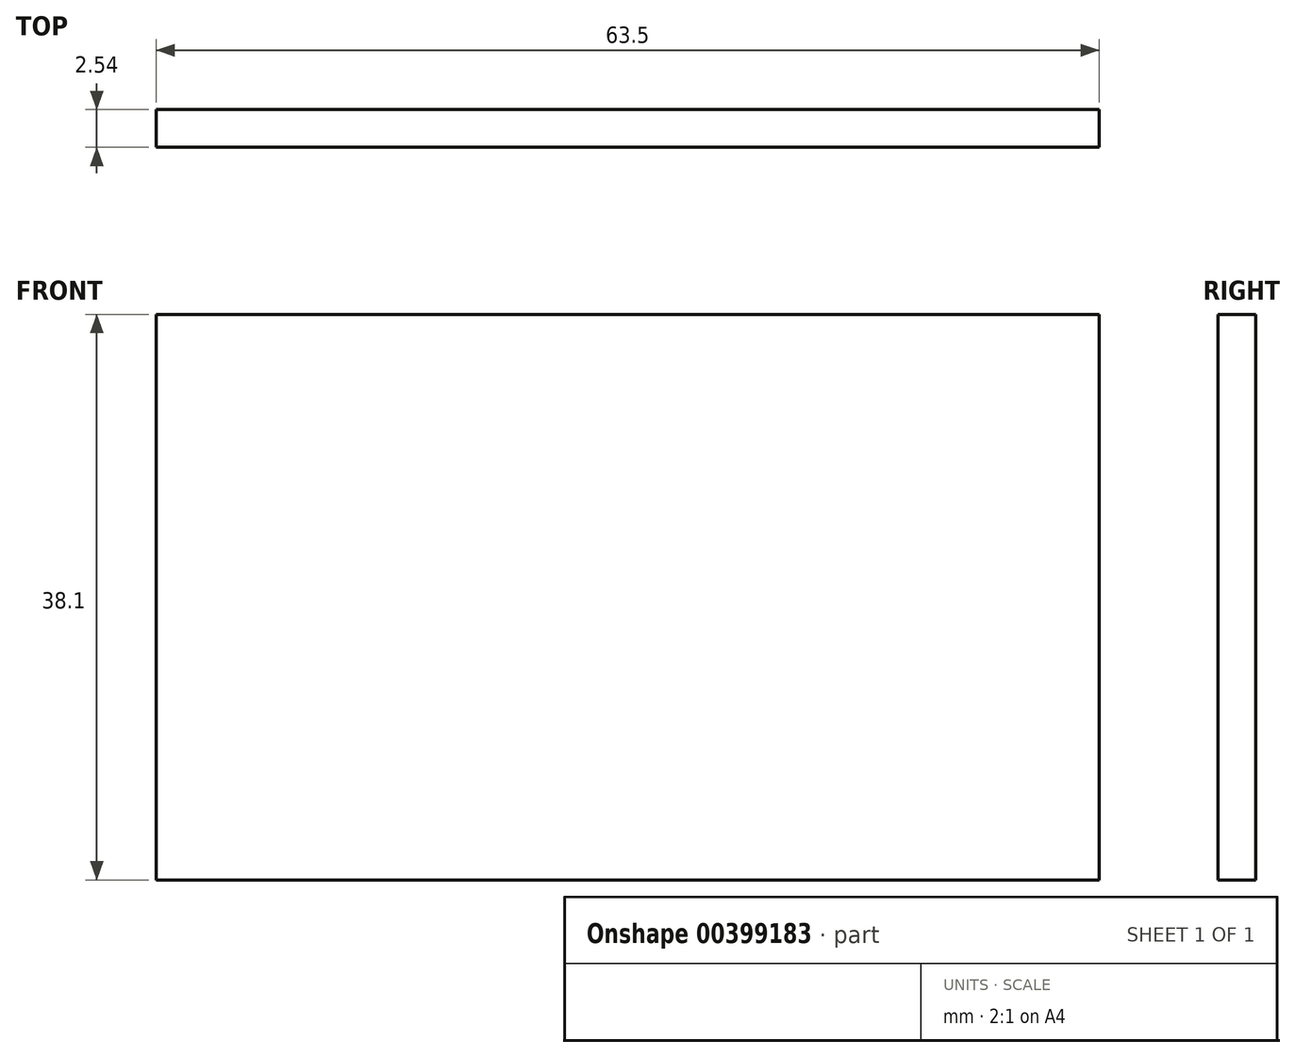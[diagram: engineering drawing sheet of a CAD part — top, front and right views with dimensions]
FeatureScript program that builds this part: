
annotation { "Feature Type Name" : "Feature", "Feature Type Description" : "" }
export const myFeature = defineFeature(function(context is Context, id is Id, definition is map)
    precondition{}
    {
        {
            var Q0;
            Q0=qCreatedBy(makeId("Front.planeOp"),FACE);
            var sketch = newSketch(context, id + "F0", { "sketchPlane" : qUnion([Q0])});
            skLineSegment(sketch, "E0.bottom", {"start": v(-31.75, 19.05) * mm, "end": v(31.75, 19.05) * mm});
            skLineSegment(sketch, "E0.top", {"start": v(-31.75, -19.05) * mm, "end": v(31.75, -19.05) * mm});
            skLineSegment(sketch, "E0.left", {"start": v(-31.75, 19.05) * mm, "end": v(-31.75, -19.05) * mm});
            skLineSegment(sketch, "E0.right", {"start": v(31.75, 19.05) * mm, "end": v(31.75, -19.05) * mm});
            skPoint(sketch, "E0.middle", {"position": v(0, 0) * mm});
            skSolve(sketch);
        }
        {
            var Q0;
            Q0=makeQuery(id+"F0.imprint","IMPRINT",FACE,{"disambiguationData":[TD([[makeQuery(id+"F0.imprint","IMPRINT",EDGE,{"derivedFrom":sQuery(id+"F0.wireOp",EDGE,"E0.bottom")}),-1.0]])]});
            extrude(context, id + "F1", {"entities" : qUnion([Q0]), "depth" : 2.54 * mm});
        }
    });
